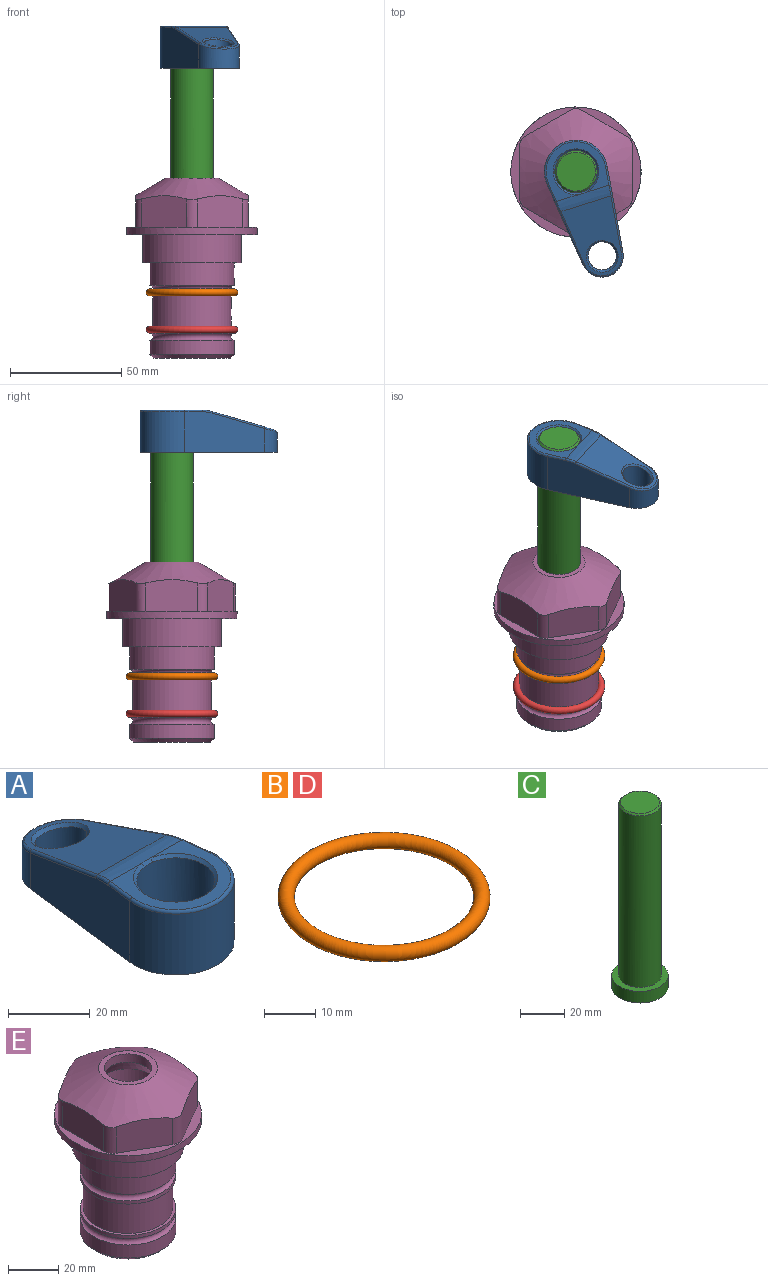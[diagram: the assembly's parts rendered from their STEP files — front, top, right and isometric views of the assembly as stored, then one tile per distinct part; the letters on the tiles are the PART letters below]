
ASSEMBLY  parts=5 mates=4
PART A: 31 faces, bbox 31.7x65.5x19.8 mm
  f0: plane 39.12x18.26mm, normal (0.99,0.12,0), area 612.2mm2, adj f1,f4,f7,f11,f13,f15
  f1: cylinder r=9.53mm len=18.91mm, axis (0,0,-1), area 296.1mm2, adj f0,f2,f7,f17
  f2: plane 39.12x18.26mm, normal (-0.99,0.12,0), area 612.2mm2, adj f1,f4,f7,f12,f14,f16
  f3: cylinder r=6.35mm len=12.7mm, axis (0,0,-1), area 362.4mm2, adj f7,f18
  f4: cylinder r=14.29mm len=28.58mm, axis (0,0,-1), area 882.2mm2, adj f0,f2,f7,f10
  f5: cylinder r=9.53mm len=19.05mm, axis (0,0,-1), area 1092.6mm2, adj f7,f19,f20
  f6: plane 26.99x23.69mm, normal (0,0,1), area 216.2mm2, adj f9,f10,f11,f12,f19
  f7: plane 63.5x28.58mm, normal (0,0,-1), area 661.8mm2, adj f0,f1,f2,f3,f4,f5,f22,f23
  f8: plane 33.52x23.6mm, normal (0,0.26,0.97), area 486mm2, adj f9,f15,f16,f17,f18
  f9: cylinder r=19.05mm len=24.72mm, axis (1,0,0), area 120.4mm2, adj f6,f8,f13,f14,f20
  f10: torus R=13.49mm, axis (0,0,1), area 59mm2, adj f4,f6,f11,f12
  f11: cylinder r=0.79mm len=8.67mm, axis (0.12,-0.99,0), area 10.8mm2, adj f0,f6,f10,f13
  f12: cylinder r=0.79mm len=8.67mm, axis (0.12,0.99,0), area 10.8mm2, adj f2,f6,f10,f14
  f13: bspline ~4.95x1.42mm, area 6.1mm2, adj f0,f9,f11,f15
  f14: bspline ~4.95x1.42mm, area 6.1mm2, adj f2,f9,f12,f16
  f15: cylinder r=0.79mm len=25.95mm, axis (0.12,-0.96,0.26), area 32.9mm2, adj f0,f8,f13,f17
  f16: cylinder r=0.79mm len=25.95mm, axis (0.12,0.96,-0.26), area 32.9mm2, adj f2,f8,f14,f17
  f17: bspline ~18.91x8.38mm, area 30mm2, adj f1,f8,f15,f16
  f18: bspline ~14.29x14.29mm, area 48.3mm2, adj f3,f8
  f19: cone r=9.53mm half-angle=45deg, axis (0,0,1), area 66.5mm2, adj f5,f6,f20
  f20: bspline ~3.22x0.96mm, area 3.5mm2, adj f5,f9,f19
  f21: plane 2.75x2.72mm, normal (0,0,-1), area 2.9mm2, adj f23,f25,f28
  f22: plane 23.05x15.88mm, normal (-0.99,-0.12,0), area 323.6mm2, adj f7,f25,f26,f27,f28,f29
  f23: plane 23.05x15.88mm, normal (0.99,-0.12,0), area 323.6mm2, adj f7,f21,f25,f27,f28,f30
  f24: cylinder r=9.53mm len=10.69mm, axis (0,0,-1), area 114.7mm2, adj f7,f27,f29,f30
  f25: cylinder r=12.7mm len=20.59mm, axis (0,0,-1), area 381.1mm2, adj f7,f21,f22,f23,f26,f28
  f26: plane 2.75x2.72mm, normal (0,0,-1), area 2.9mm2, adj f22,f25,f28
  f27: plane 19.72x18.37mm, normal (0,-0.26,-0.97), area 291.8mm2, adj f22,f23,f24,f28,f29,f30
  f28: cylinder r=15.88mm len=19.92mm, axis (1,0,0), area 54.8mm2, adj f21,f22,f23,f25,f26,f27
  f29: cylinder r=1.59mm len=11mm, axis (0,0,-1), area 34.7mm2, adj f7,f22,f24,f27
  f30: cylinder r=1.59mm len=11mm, axis (0,0,-1), area 34.7mm2, adj f7,f23,f24,f27
PART B: 1 faces, bbox 44.7x44.7x3.2 mm
  f0: torus R=19.05mm, axis (0,0,1), area 1193.9mm2
PART C: 6 faces, bbox 25.4x25.4x101.6 mm
  f0: plane 17.46x17.46mm, normal (0,0,1), area 239.5mm2, adj f5
  f1: plane 25.4x25.4mm, normal (0,0,-1), area 506.7mm2, adj f2
  f2: cylinder r=12.7mm len=25.4mm, axis (0,0,1), area 506.7mm2, adj f1,f3
  f3: plane 25.4x25.4mm, normal (0,0,1), area 221.7mm2, adj f2,f4
  f4: cylinder r=9.53mm len=94.46mm, axis (0,0,1), area 5653mm2, adj f3,f5
  f5: cone r=8.73mm half-angle=45deg, axis (0,0,-1), area 64.4mm2, adj f0,f4
PART D: same geometry as B
PART E: 36 faces, bbox 58.7x58.7x81 mm
  f0: cylinder r=17.78mm len=35.56mm, axis (0,0,1), area 1670.8mm2, adj f23,f24,f31
  f1: cylinder r=19.05mm len=38.1mm, axis (0,0,1), area 1191.9mm2, adj f26,f27,f30
  f2: plane 58.66x58.66mm, normal (0,0,-1), area 1150.6mm2, adj f3,f28
  f3: cylinder r=29.33mm len=58.66mm, axis (0,0,-1), area 585.1mm2, adj f2,f4
  f4: plane 58.66x58.66mm, normal (0,0,1), area 475.9mm2, adj f3,f5,f6,f7,f8,f9,f10,f11
  f5: plane 20.32x14.34mm, normal (-0.5,0.87,0), area 324.4mm2, adj f4,f15,f16,f17
  f6: plane 20.32x14.34mm, normal (0.5,0.87,0), area 324.4mm2, adj f4,f14,f15,f17
  f7: plane 23.48x14.34mm, normal (1,0,0), area 324.4mm2, adj f4,f13,f14,f17
  f8: plane 20.32x14.34mm, normal (0.5,-0.87,0), area 324.4mm2, adj f4,f12,f13,f17
  f9: plane 20.32x14.34mm, normal (-0.5,-0.87,0), area 324.4mm2, adj f4,f11,f12,f17
  f10: plane 23.48x14.34mm, normal (-1,0,0), area 324.4mm2, adj f4,f11,f16,f17
  f11: cylinder r=5.08mm len=12.85mm, axis (0,0,-1), area 67.2mm2, adj f4,f9,f10,f17
  f12: cylinder r=5.08mm len=12.85mm, axis (0,0,-1), area 67.2mm2, adj f4,f8,f9,f17
  f13: cylinder r=5.08mm len=12.85mm, axis (0,0,-1), area 67.2mm2, adj f4,f7,f8,f17
  f14: cylinder r=5.08mm len=12.85mm, axis (0,0,-1), area 67.2mm2, adj f4,f6,f7,f17
  f15: cylinder r=5.08mm len=12.85mm, axis (0,0,-1), area 67.2mm2, adj f4,f5,f6,f17
  f16: cylinder r=5.08mm len=12.85mm, axis (0,0,-1), area 67.2mm2, adj f4,f5,f10,f17
  f17: cone r=11.73mm half-angle=60deg, axis (0,0,-1), area 2071.8mm2, adj f5,f6,f7,f8,f9,f10,f11,f12
  f18: plane 23.46x23.46mm, normal (0,0,1), area 147.4mm2, adj f17,f35
  f19: plane 34.93x34.93mm, normal (0,0,-1), area 958mm2, adj f29
  f20: cylinder r=19.05mm len=38.1mm, axis (0,0,1), area 760.1mm2, adj f21,f29
  f21: torus R=19.05mm, axis (0,0,1), area 565.3mm2, adj f20,f22
  f22: cylinder r=19.05mm len=38.1mm, axis (0,0,1), area 190mm2, adj f21,f23
  f23: plane 38.1x38.1mm, normal (0,0,1), area 146.9mm2, adj f0,f22
  f24: plane 38.1x38.1mm, normal (0,0,-1), area 146.9mm2, adj f0,f25
  f25: cylinder r=19.05mm len=38.1mm, axis (0,0,1), area 190mm2, adj f24,f26
  f26: torus R=19.05mm, axis (0,0,1), area 565.3mm2, adj f1,f25
  f27: plane 44.45x44.45mm, normal (0,0,-1), area 411.7mm2, adj f1,f28
  f28: cylinder r=22.23mm len=44.45mm, axis (0,0,1), area 1773.5mm2, adj f2,f27
  f29: cone r=19.05mm half-angle=45deg, axis (0,0,1), area 257.5mm2, adj f19,f20
  f30: cylinder r=3.17mm len=6.75mm, axis (-1,0,0), area 128mm2, adj f1,f33
  f31: cylinder r=3.17mm len=6.35mm, axis (-1,0,0), area 102.5mm2, adj f0,f33
  f32: plane 25.4x25.4mm, normal (0,0,1), area 506.7mm2, adj f33
  f33: cylinder r=12.7mm len=66.42mm, axis (0,0,-1), area 5236.2mm2, adj f30,f31,f32,f34
  f34: cone r=9.53mm half-angle=30deg, axis (0,0,-1), area 443.4mm2, adj f33,f35
  f35: cylinder r=9.53mm len=19.05mm, axis (0,0,-1), area 240.9mm2, adj f18,f34
PLACE A rot(axis=(0,0,-1),162.7deg) t=(0,0,30.41)mm
PLACE B t=(0,0,-1.59)mm
PLACE C rot(axis=(0,0,-1),162.7deg) t=(0,0,30.41)mm
PLACE D t=(0,0,-18.41)mm
PLACE E at identity fixed
MATE fastened D.f0 <-> E.f0  axis (0,0,1) through (0,0,-42.93)mm
MATE cylindrical C.f2 <-> E.f0  axis (0,0,-1) through (0,0,-7.69)mm
MATE fastened B.f0 <-> E.f0  axis (0,0,1) through (0,0,-26.1)mm
MATE fastened C.f2 <-> A.f4  axis (0,0,1) through (0,0,93.91)mm
